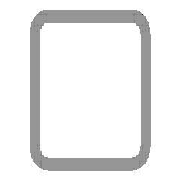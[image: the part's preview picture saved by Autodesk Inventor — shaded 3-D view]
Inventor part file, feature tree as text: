
AUTODESK INVENTOR PART (.ipt)
format: ipt  version: 2025 (Build 290162010, 162A)  size: 134,656 bytes
history: native  units: mm (DEFAULTED — no unit token found)
features: other x4, sketch x1, plane x1
ambient origin geometry x8: Origin, YZ Plane, XZ Plane, XY Plane, X Axis, Y Axis, Z Axis, Center Point
bodies: Solid1 (feature_tree), Body (feature_tree)
feature tree (6):
  parser-record x1  (decoder bookkeeping rows leaked as tree rows — omitted from the tree; the rows remain in map.json)
  other  "Driven Length"
  other  "Start Plane"
  other  "End Plane"
  sketch  "Sketch3"  dims[d3=1420.0mm d4=0.0mm d7=4.0mm d9=40.0mm d11=40.0mm d12=2.0mm d13=40.0mm d14=1460.0mm d15=20.0mm d16=20.0mm d17=90.0deg d18=1420.0mm]
  plane  "Work Plane3"
